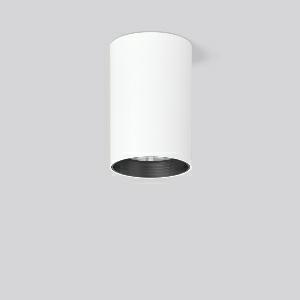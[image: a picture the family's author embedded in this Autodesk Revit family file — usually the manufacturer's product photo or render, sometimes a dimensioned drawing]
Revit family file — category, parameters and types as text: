
# Revit family: heledon_maxi_a_931227_002_2_76_2f56
name_source: partatom
category: Lighting Fixtures
units: mm (PartAtom-declared; Revit-internal decimal feet)

## family parameters
Cut with Voids When Loaded = No
Host = Face
Light Source = No
Part Type = Normal
Room Calculation Point = No
Round Connector Dimension = Use Diameter
Shared = No

## types (1)
- HELEDON maxi A (1 x LED Modul 927, 3500 lm, 2700)
    Apparent Load = 35 VA
    Approval mark = CE
    CIE Flux Codes = 97 100 100 100 100
    Color Rendering = 92
    Color Temperature = 2700
    Default Elevation = 1800 mm
    Description = Series: HELEDON maxi
Cylindrical surface-mounted downlight. Housing: die-cast aluminium, powder-coated. Internal ceiling frame polycarbonate with bayonet mounting. Black plastic ring and recessed LED to prevent glare from the side. Optical assembly with lens made of plastic (polycarbonate) for the best homogeneous light distribution - can be changed without tools. Best colour rendering index Ra>90. Suitable for Ceiling mounting. Easy installation with a separate ceiling frame with bayonet mounting and plug connection. Driver integrated. Connected via plug-in connector. High quality converter without flickering and stroboscopic effect. The following accessories can be mounted without use of tools: interchangeable lenses, decorative glasses, honeycomb louvre, clear and frosted diffusers, white interchangeable plastic ring. 
Colour: traffic white, matt (RAL 9016)
Diameter: 123 mm
Height: 183 mm
Lamp: LED
Socket: without socket
Colour temperature: 2700K
Colour rendering index (CRI): 92
System power: 35 W
Rated luminous flux: 3500 lm
Luminous efficiency: 100 lm/W
Control gear: Converter, dimmable, DALI
Protection class: I
Type of protection: IP 20
    Height = 183 mm
    Lamp = 1 x LED Modul 927
    Lamp Light Flux = 3500 lm
    Lamp count = 1
    Length = 123 mm
    Lifetime = 50000 h
    Luminous efficacy = 100 lm/W
    Manufacturer = RZB
    ModVariant = No
    Model = 931227.002.2.76
    Mounting Place = Ceiling
    Mounting Type = Surface mounted
    Number of Poles = 1
    OnlyDefault = Yes
    Power Factor = 1
    Product Name = HELEDON maxi A
    Product group = Surface mounted downlights
    ProductGroupID = 302
    Protection Class = Protection class I
    Protection Degree = IP 20
    RLX_Detail_Level = 1
    RLX_Emergency_Light_Flux = 0 lm
    RLX_Emergency_Type = 0
    RLX_Emergency_Type_DB = No
    RlxData = <blob elided: 96589 chars, md5=758eee2d>
    Socket = socket
    Standby Power = 0 W
    System Light Flux = 3500 lm
    System Power = 35 W
    Type Comments = Product without accessories
    Type Image = 931193.002.jpg
    URL = http://relux.com
    VarID = ---
    Voltage = 230 V
    Voltage Range = 220-240 V
    Weight = 0.00 kg
    Width = 0 mm  [stored 0 ft]

note: [stored X ft] marks values corroborated as IEEE doubles in the binary element streams (Revit-internal decimal feet)

## geometry (parser evidence)
native form markers: Blend x4, Sweep x11
no freeform markers — native parametric forms only
